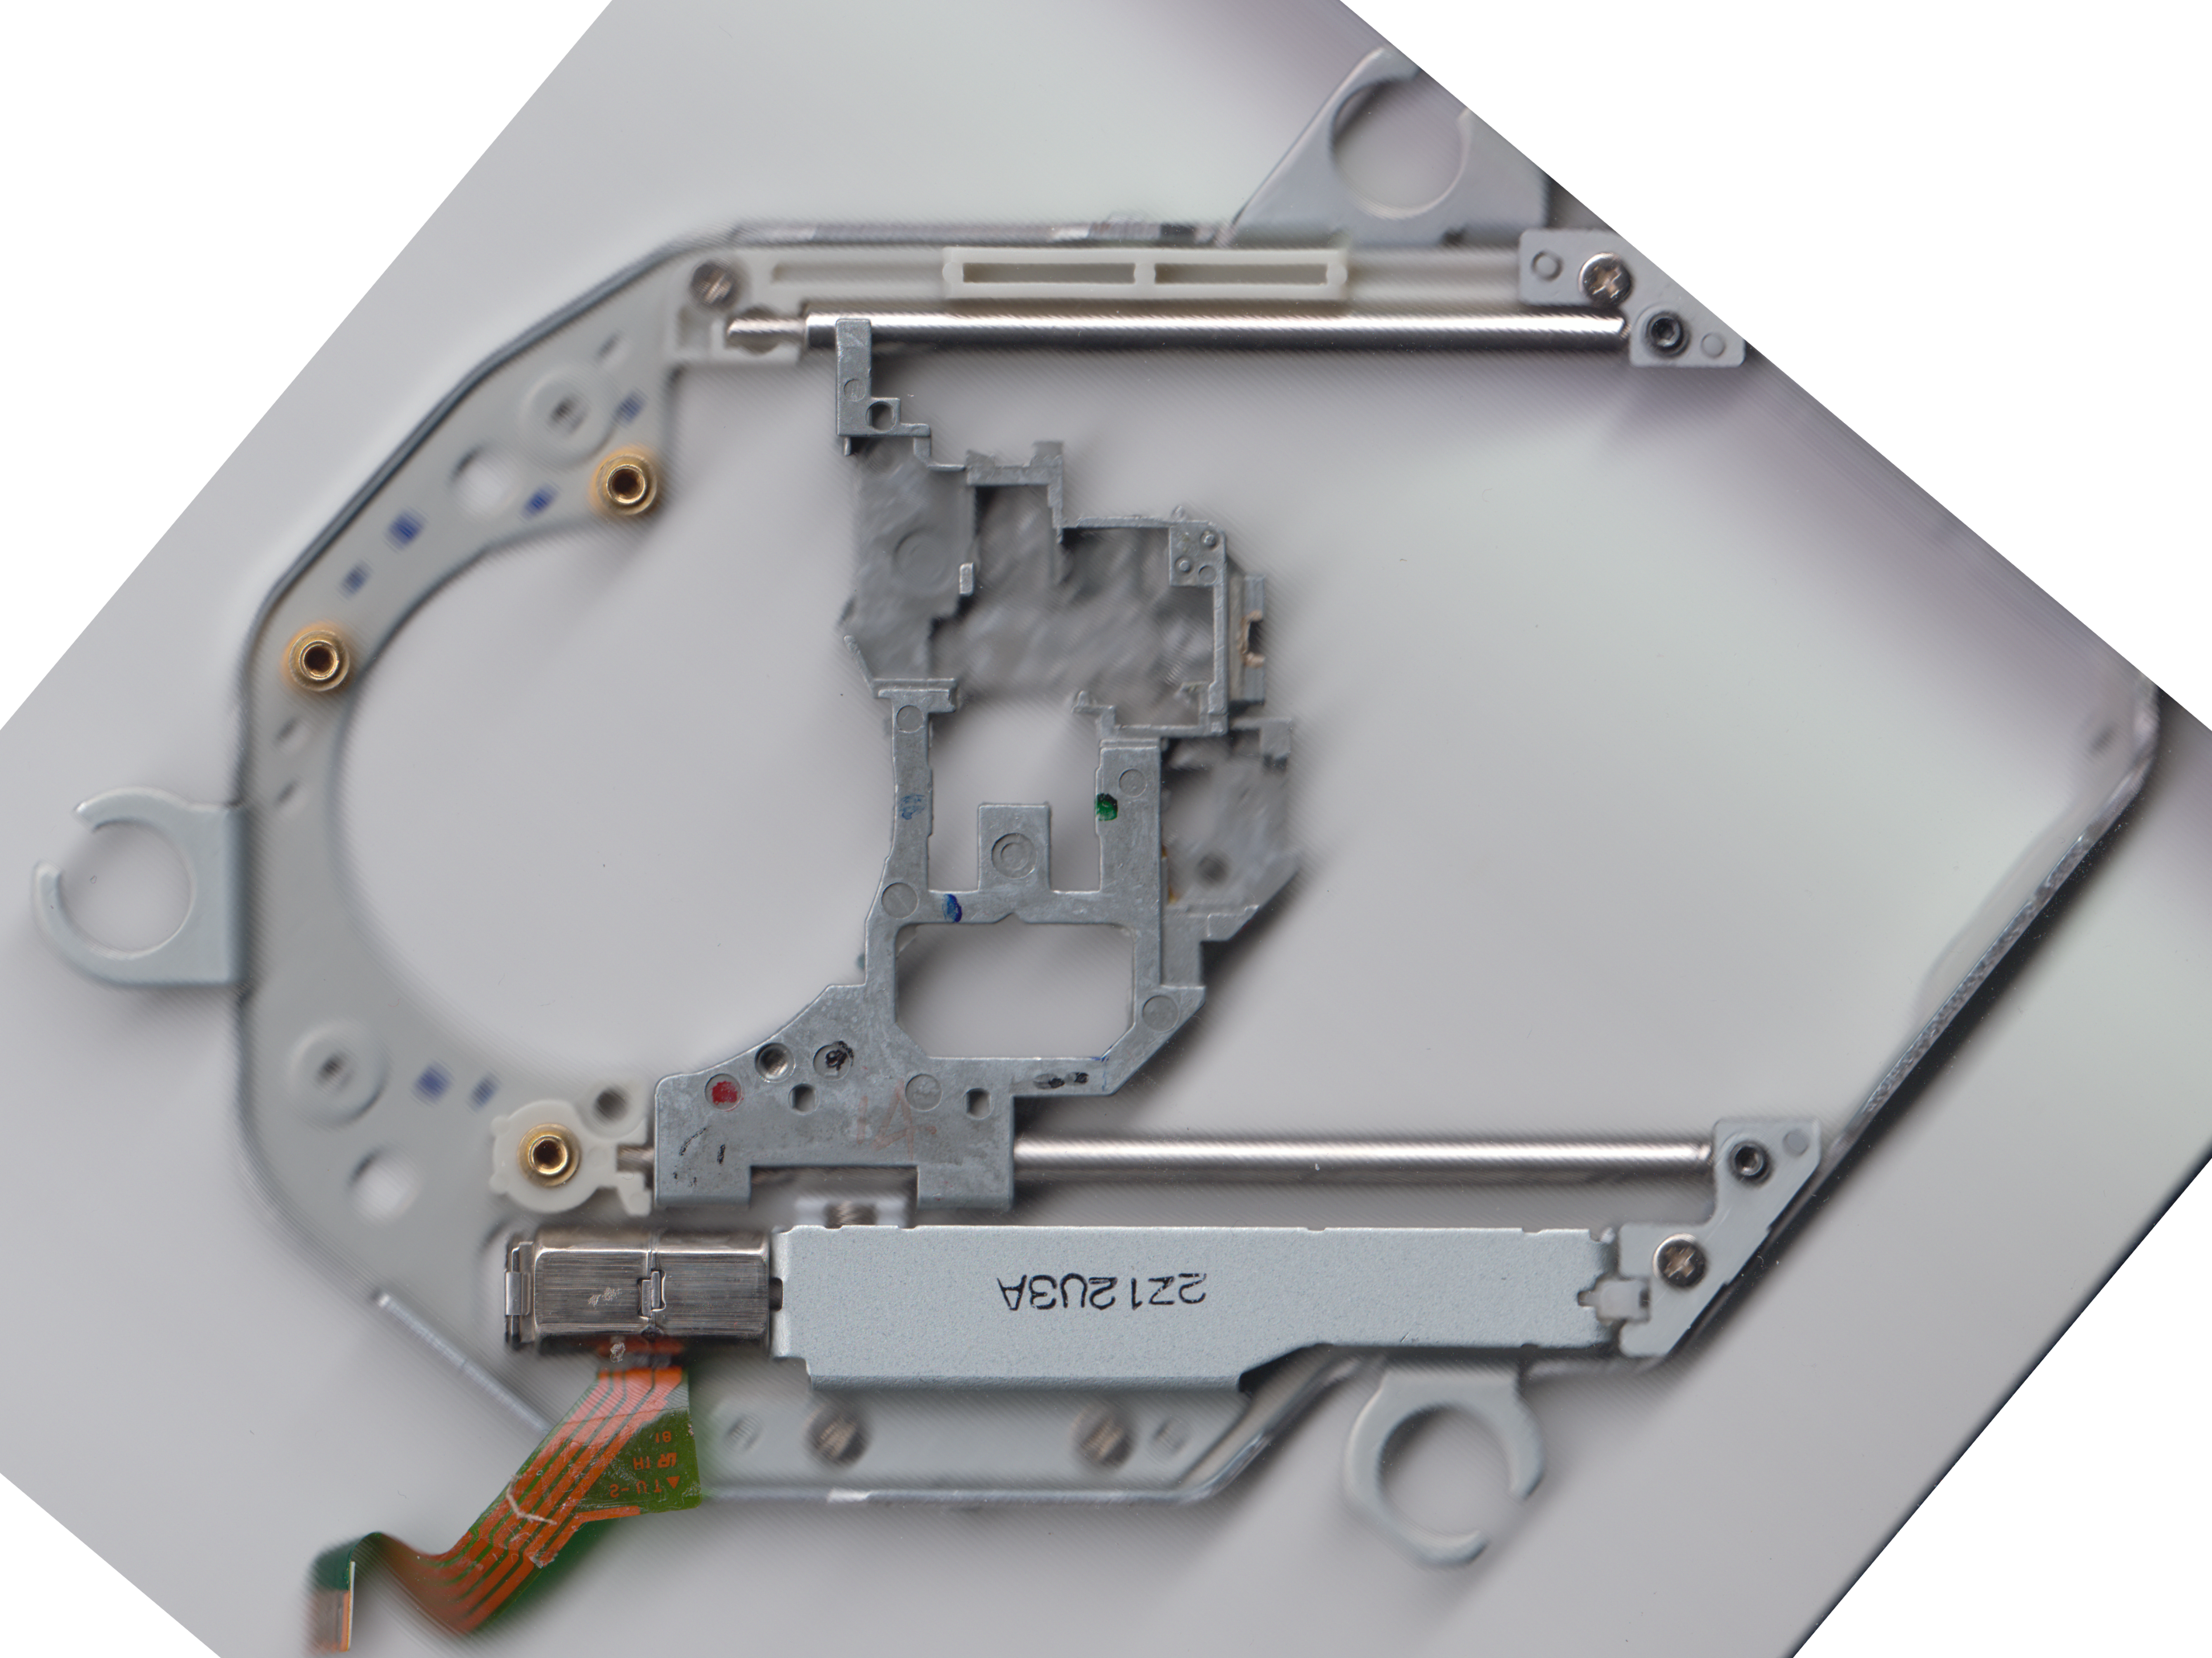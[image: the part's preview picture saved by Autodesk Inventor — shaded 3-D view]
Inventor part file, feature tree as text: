
AUTODESK INVENTOR PART (.ipt)
format: ipt  version: 2021 (Build 250183000, 183)  size: 8,675,328 bytes
history: native  units: mm
features: extrude x3, other x2, reference x1
ambient origin geometry x8: Origin, YZ Plane, XZ Plane, XY Plane, X Axis, Y Axis, Z Axis, Center Point
bodies: Body1 (feature_tree)
feature tree (6):
  reference  "reference"
  other  "carriage"
  extrude  "carriage_narrow"  Depth=30.0mm
  extrude  "carriage_wide"  Depth=7.1mm
  extrude  "carriage_thinner"  Depth=7.1mm
  other  "Image2"
